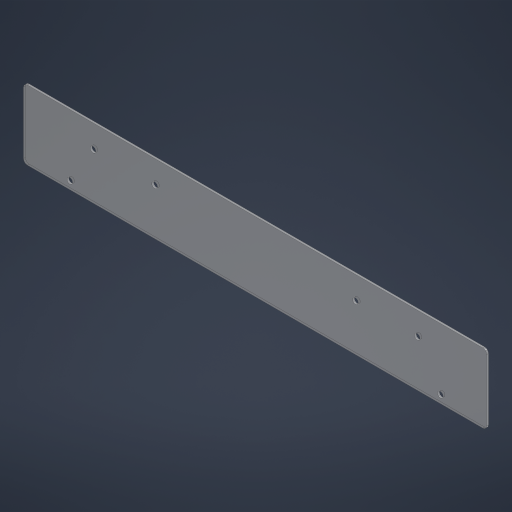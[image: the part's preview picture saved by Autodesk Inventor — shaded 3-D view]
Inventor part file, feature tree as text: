
AUTODESK INVENTOR PART (.ipt)
format: ipt  version: 2024 (Build 280153000, 153)  size: 222,720 bytes
history: native  units: in
note: dims shown in document units (in); Inventor stores cm internally (conversion verified against a paired STEP export)
features: sketch x2, extrude x1, hole x1
ambient origin geometry x8: Origin, YZ Plane, XZ Plane, XY Plane, X Axis, Y Axis, Z Axis, Center Point
bodies: Solid1 (feature_tree)
feature tree (4):
  extrude  "Extrusion1"  Depth=0.0625in TaperAngle=0.0deg
  hole  "Hole1"  [1 undecoded]
  sketch  "Sketch1"  dims[d1=2.0in d2=0.0625in d3=0.0in]
  sketch  "Sketch2"  dims[d4=2.25in d5=2.0in d6=0.75in d7=0.25in d11=1.5in d12=0.1875in d13=0.75in d14=0.375in d15=0.25in d16=0.5635in d17=1.0in d18=0.8108in d19=0.125in d20=0.125in]
note: 1 required parameter value undecoded (feature->parameter linkage not recoverable at this tier; creation-order binding heuristic only, values carry confidence <= 0.55)
